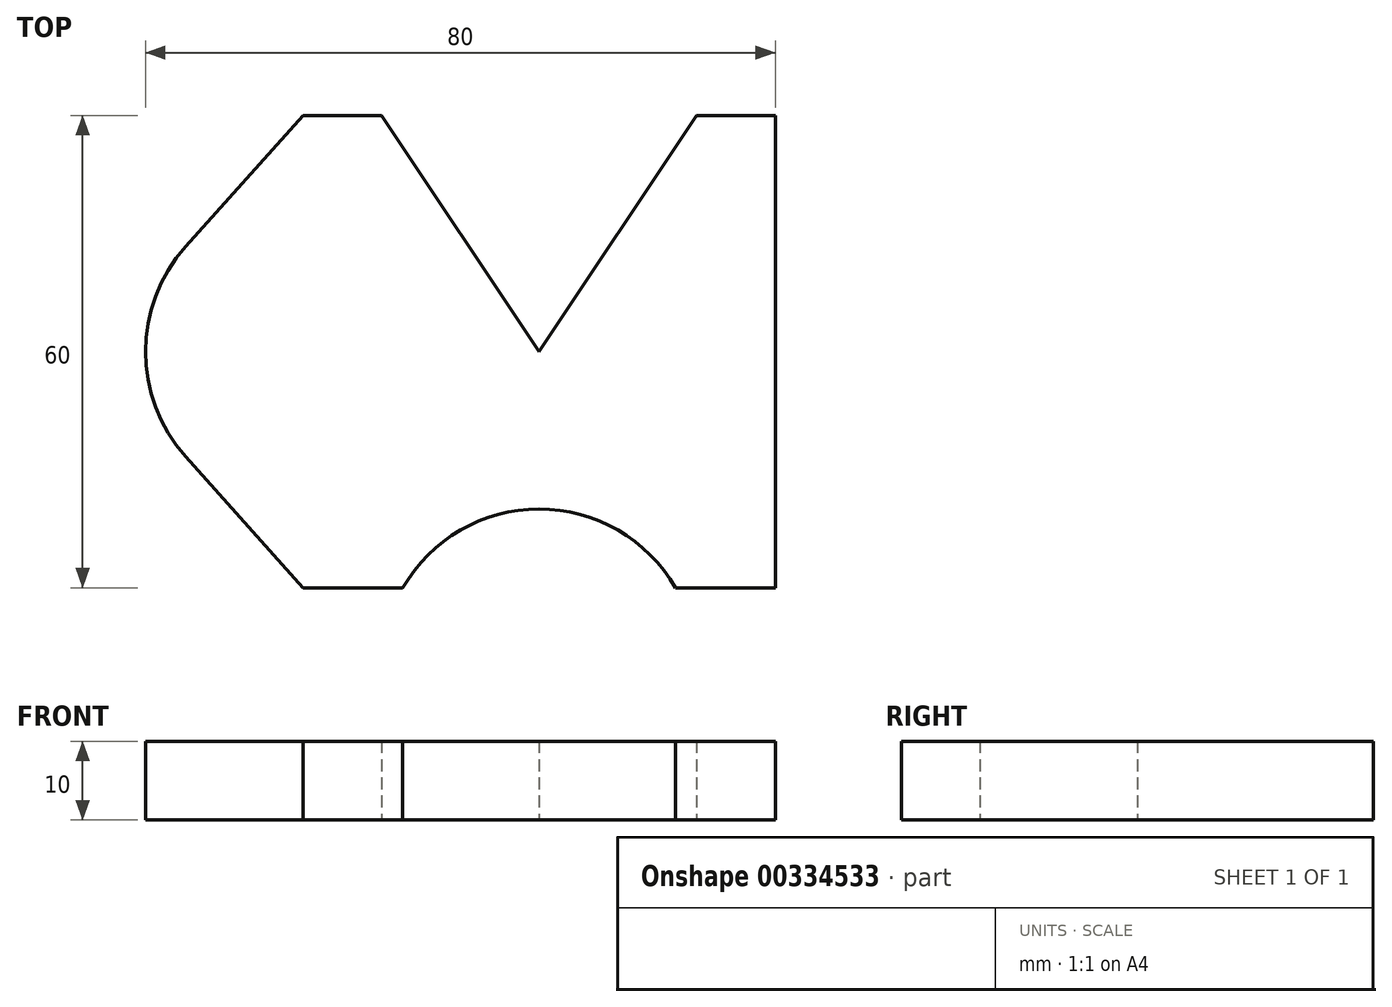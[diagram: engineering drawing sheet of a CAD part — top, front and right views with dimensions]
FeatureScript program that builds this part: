
annotation { "Feature Type Name" : "Feature", "Feature Type Description" : "" }
export const myFeature = defineFeature(function(context is Context, id is Id, definition is map)
    precondition{}
    {
        {
            var Q0;
            Q0=qCreatedBy(makeId("Top.planeOp"),FACE);
            var sketch = newSketch(context, id + "F0", { "sketchPlane" : qUnion([Q0])});
            skLineSegment(sketch, "E0", {"start": v(0, 0) * mm, "end": v(20, 30) * mm});
            skLineSegment(sketch, "E1", {"start": v(20, 30) * mm, "end": v(30, 30) * mm});
            skLineSegment(sketch, "E2", {"start": v(30, 30) * mm, "end": v(30, -30) * mm});
            skLineSegment(sketch, "E3", {"start": v(30, -30) * mm, "end": v(-30, -30) * mm});
            skCircle(sketch, "E4", {"center": v(0, -40) * mm, "radius": 20 * mm});
            skCircle(sketch, "E5", {"center": v(-30, 0) * mm, "radius": 20 * mm});
            skLineSegment(sketch, "E6", {"start": v(-30, -30) * mm, "end": v(-44.9, -13.33) * mm});
            skLineSegment(sketch, "E7", {"start": v(0, 0) * mm, "end": v(-20, 30) * mm});
            skLineSegment(sketch, "E8", {"start": v(-20, 30) * mm, "end": v(-30, 30) * mm});
            skLineSegment(sketch, "E9", {"start": v(-30, 30) * mm, "end": v(-44.9, 13.33) * mm});
            skSolve(sketch);
        }
        {
            var Q0;
            Q0=makeQuery(id+"F0.imprint","IMPRINT",FACE,{"disambiguationData":[TD([[makeQuery(id+"F0.imprint","IMPRINT",EDGE,{"derivedFrom":sQuery(id+"F0.wireOp",EDGE,"E0")}),-1.0]])]});
            var Q1;
            {var subQ0=sQuery(id+"F0.wireOp",EDGE,"E5");var subQ1=makeQuery(id+"F0.imprint","INTERSECT",VERTEX,{"derivedFrom":[subQ0,sQuery(id+"F0.wireOp",EDGE,"E6")]});Q1=makeQuery(id+"F0.imprint","IMPRINT",FACE,{"disambiguationData":[TD([[makeQuery(id+"F0.imprint","IMPRINT",EDGE,{"disambiguationData":[TD([[subQ1,1.0]])],"derivedFrom":subQ0}),1.0]])]});}
            extrude(context, id + "F1", {"entities" : qUnion([Q0, Q1]), "depth" : 10 * mm});
        }
    });
